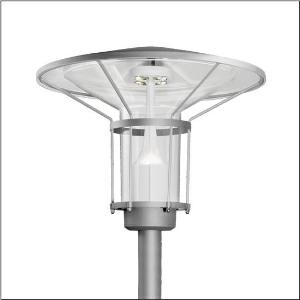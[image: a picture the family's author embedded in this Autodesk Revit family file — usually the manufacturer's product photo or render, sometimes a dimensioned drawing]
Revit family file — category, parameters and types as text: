
# Revit family: laterne_classic_iq___st1_2a_5xa5245ef14hp_6e9b
name_source: partatom
category: Lighting Fixtures
units: mm (PartAtom-declared; Revit-internal decimal feet)

## family parameters
Cut with Voids When Loaded = No
Host = Face
Light Source = No
Part Type = Normal
Room Calculation Point = No
Round Connector Dimension = Use Diameter
Shared = No

## types (1)
- --- (1 x LED, 4240 lm, 33.6 W, 3000K)
    Apparent Load = 34 VA
    CIE Flux Codes = 22 60 93 98 100
    Color Rendering = 70
    Color Temperature = 3000K
    Default Elevation = 1800 mm
    Description = Lantern Classic iQ, mast luminaire, Module 540 iQ-SR, primary light control with 3 zone facetted reflector, of plastic, silver coated, highly specular, structured, primary optical cover: cover, of PMMA, transparent, light distribution: ST1.2a, light emission: direct distribution, primary light characteristic: asymmetric, installation type: post-top, LED, High Power LED, rated luminous flux: 4.240lm, luminous efficacy: 126lm/W, light colour: 730, colour temperature: 3000K, control gear: ECG iQ, control: presetting dimming logarithmic, Street-Remote, Auto-Match, Temp-Guard, Lumen-Switch, Night-Set, Smart-Wire, Light-Fading, Desk-Remote (wireless, voltage-free reading and setting of iQ features in the workshop via application-optimized NFC function/RFID function), optimised constant luminous flux control (CLO 2.0), with terminal, 6-pole, max. 2.5mm², mains connection: 230..240V, AC, 50/60Hz, start of lifetime: 34W, end of service life: 36W, reduction: 15W, luminaire housing, upper part, of glass-fibre reinforced polyester, coated, Siteco® metallic grey (DB 702S), diameter: 750mm, height: 596mm, spigot size: d x l = 76 x 70mm (post-top) | with reducer (optional accessory) 60 x 70mm, post-top mast mounting element, of diecast aluminium, coated, Siteco® metallic grey (DB 702S), Module 540 iQ-SR, traffic white (RAL 9016), equipment: Power, protection rating (complete): IP65, insulation class (complete): insulation class II (safety insulation), certification: CE, ENEC, VDE, packaging unit: 1 piece

Light Distribution: ST1.2a
    Height = 596 mm
    Lamp = 1 x LED
    Lamp Light Flux = 4240 lm
    Lamp Power = 33.6 W
    Lamp count = 1
    Length = 750 mm
    Luminous efficacy = 126 lm/W
    Manufacturer = Siteco
    ModVariant = No
    Model = 5XA5245EF14HP
    Number of Poles = 1
    OnlyDefault = Yes
    Power Factor = 1
    Product Name = Laterne Classic iQ | ST1.2a
    Product group = mast luminaire | pylon top
    ProductGroupID = 6100
    Protection Class = Protection class II
    Protection Degree = IP 65
    RLX_Detail_Level = 1
    RLX_Emergency_Light_Flux = 0 lm
    RLX_Emergency_Type = 0
    RLX_Emergency_Type_DB = No
    RlxData = <blob elided: 65069 chars, md5=80180bf8>
    Socket = socket
    Standby Power = 0 W
    System Light Flux = 4240 lm
    System Power = 34 W
    Type Comments = factory setting: luminous flux: 100 % | dim-lin: 254 | 695 mA
    Type Image = l_1006052.jpg
    URL = http://relux.com
    VarID = @adj_145923
    Voltage = 0 V
    Weight = 0.00 kg
    Width = 0 mm  [stored 0 ft]

note: [stored X ft] marks values corroborated as IEEE doubles in the binary element streams (Revit-internal decimal feet)

## geometry (parser evidence)
native form markers: Blend x4, Sweep x8
no freeform markers — native parametric forms only
